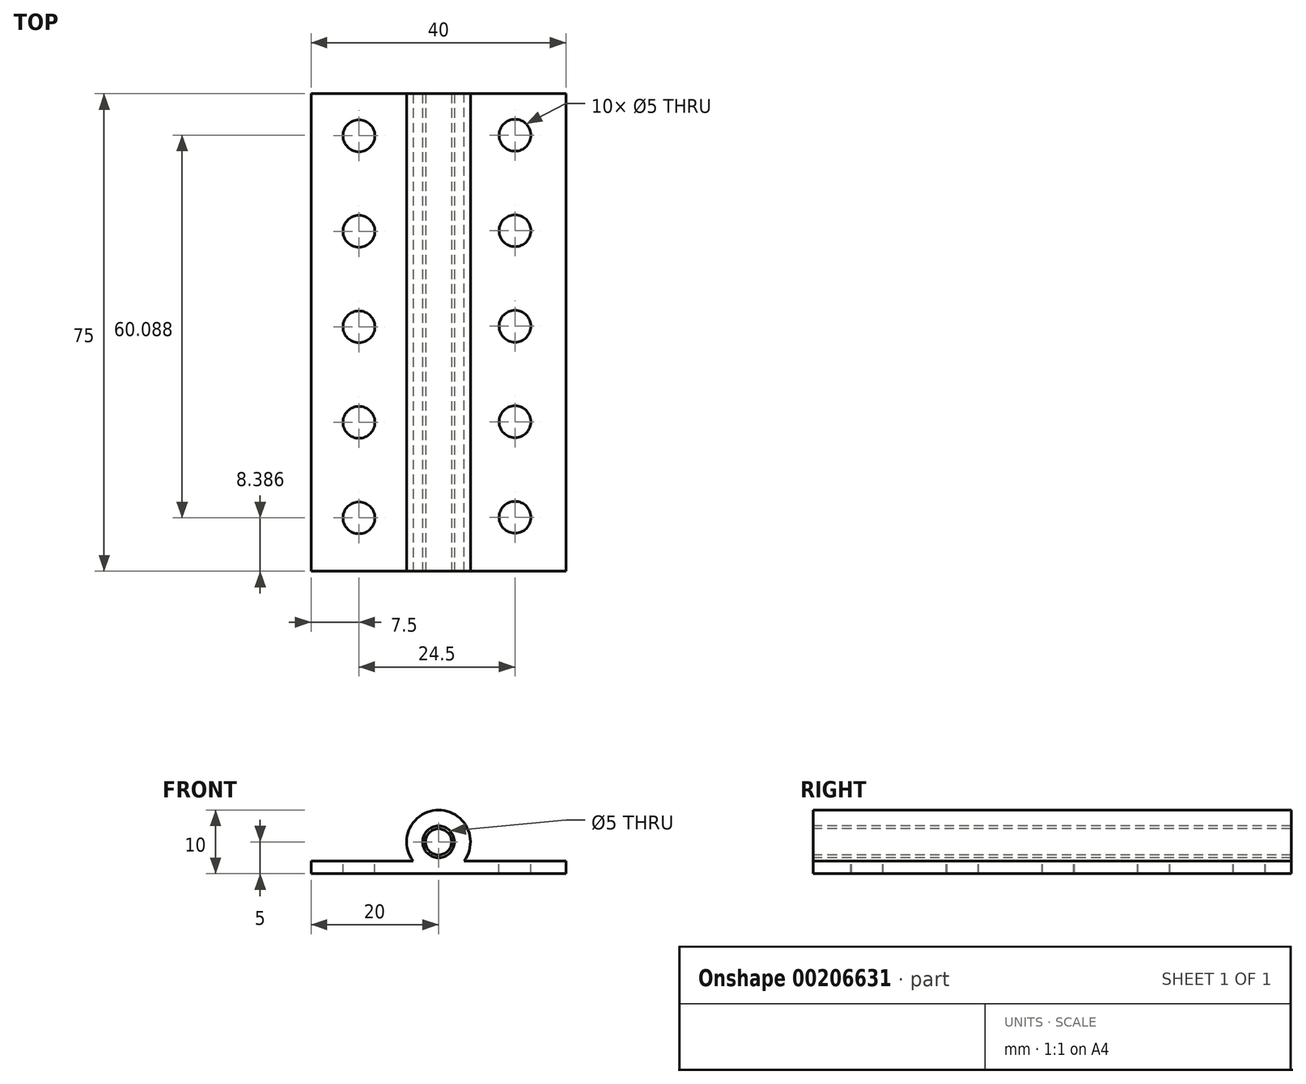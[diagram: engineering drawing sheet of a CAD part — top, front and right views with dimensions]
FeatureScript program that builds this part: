
annotation { "Feature Type Name" : "Feature", "Feature Type Description" : "" }
export const myFeature = defineFeature(function(context is Context, id is Id, definition is map)
    precondition{}
    {
        {
            var Q0;
            Q0=qCreatedBy(makeId("Front.planeOp"),FACE);
            var sketch = newSketch(context, id + "F0", { "sketchPlane" : qUnion([Q0])});
            skCircle(sketch, "E0", {"center": v(0, 0) * mm, "radius": 5 * mm});
            skSolve(sketch);
        }
        {
            var Q0;
            Q0=qCreatedBy(makeId("Front.planeOp"),FACE);
            var sketch = newSketch(context, id + "F1", { "sketchPlane" : qUnion([Q0])});
            skLineSegment(sketch, "E1.bottom", {"start": v(0, -5) * mm, "end": v(20, -5) * mm});
            skLineSegment(sketch, "E1.top", {"start": v(0, -3) * mm, "end": v(20, -3) * mm});
            skLineSegment(sketch, "E1.left", {"start": v(0, -5) * mm, "end": v(0, -3) * mm});
            skLineSegment(sketch, "E1.right", {"start": v(20, -5) * mm, "end": v(20, -3) * mm});
            skSolve(sketch);
        }
        {
            var Q0;
            Q0=makeQuery(id+"F0.imprint","IMPRINT",FACE,{"disambiguationData":[TD([[makeQuery(id+"F0.imprint","IMPRINT",EDGE,{"derivedFrom":sQuery(id+"F0.wireOp",EDGE,"E0")}),1.0]])]});
            var Q1;
            Q1=makeQuery(id+"F1.imprint","IMPRINT",FACE,{"disambiguationData":[TD([[makeQuery(id+"F1.imprint","IMPRINT",EDGE,{"derivedFrom":sQuery(id+"F1.wireOp",EDGE,"E1.bottom")}),1.0]])]});
            extrude(context, id + "F2", {"entities" : qUnion([Q0, Q1]), "depth" : 25 * mm});
        }
        {
            var Q0;
            Q0=makeQuery(id+"F2.opExtrude","CAP_FACE",FACE,{"disambiguationData":[OSD([sQuery(id+"F1.wireOp",EDGE,"E1.bottom"),sQuery(id+"F1.wireOp",EDGE,"E1.top"),sQuery(id+"F1.wireOp",EDGE,"E1.left"),sQuery(id+"F1.wireOp",EDGE,"E1.right")])],"isStart":false});
            extrude(context, id + "F3", {"entities" : qUnion([Q0]), "operationType" : NewBodyOperationType.ADD, "depth" : 25 * mm});
        }
        {
            var Q0;
            Q0=makeQuery(id+"F3.opExtrude","CAP_FACE",FACE,{"disambiguationData":[OSD([sQuery(id+"F1.wireOp",EDGE,"E1.bottom"),sQuery(id+"F1.wireOp",EDGE,"E1.top"),sQuery(id+"F1.wireOp",EDGE,"E1.left"),sQuery(id+"F1.wireOp",EDGE,"E1.right")])],"isStart":false});
            var sketch = newSketch(context, id + "F4", { "sketchPlane" : qUnion([Q0])});
            skCircle(sketch, "E2", {"center": v(0, 0) * mm, "radius": 5 * mm});
            skSolve(sketch);
        }
        {
            var Q0;
            {var subQ1=makeQuery(id+"F3.opExtrude","CAP_EDGE",EDGE,{"disambiguationData":[OSD([sQuery(id+"F1.wireOp",EDGE,"E1.bottom")])],"isStart":false});Q0=makeQuery(id+"F4.imprint","IMPRINT",FACE,{"disambiguationData":[TD([[makeQuery(id+"F4.imprint","IMPRINT",EDGE,{"derivedFrom":subQ1}),1.0]])]});}
            extrude(context, id + "F5", {"entities" : qUnion([Q0]), "operationType" : NewBodyOperationType.ADD, "depth" : 25 * mm});
        }
        {
            var Q0;
            Q0=qSketchRegion(id+"F4",true);
            extrude(context, id + "F6", {"entities" : qUnion([Q0]), "operationType" : NewBodyOperationType.ADD, "depth" : 25 * mm});
        }
        {
            var Q0;
            {var subQ0=sQuery(id+"F4.wireOp",EDGE,"E2");Q0=makeQuery(id+"F6.boolean.opBoolean","MERGE",FACE,{"derivedFrom":[makeQuery(id+"F5.opExtrude","CAP_FACE",FACE,{"disambiguationData":[OSD([sQuery(id+"F1.wireOp",EDGE,"E1.bottom"),sQuery(id+"F1.wireOp",EDGE,"E1.top"),sQuery(id+"F1.wireOp",EDGE,"E1.right"),subQ0])],"isStart":false}),makeQuery(id+"F6.opExtrude","CAP_FACE",FACE,{"disambiguationData":[OSD([subQ0])],"isStart":false})]});}
            var sketch = newSketch(context, id + "F7", { "sketchPlane" : qUnion([Q0])});
            skCircle(sketch, "E3", {"center": v(0, 0) * mm, "radius": 2.5 * mm});
            skSolve(sketch);
        }
        {
            var Q0;
            Q0=makeQuery(id+"F7.imprint","IMPRINT",FACE,{"disambiguationData":[TD([[makeQuery(id+"F7.imprint","IMPRINT",EDGE,{"derivedFrom":sQuery(id+"F7.wireOp",EDGE,"E3")}),1.0]])]});
            var Q1;
            Q1=sQuery(id+"F7.wireOp",EDGE,"E3");
            extrude(context, id + "F8", {"entities" : qUnion([Q0]), "operationType" : NewBodyOperationType.REMOVE, "surfaceEntities" : qUnion([Q1]), "oppositeDirection" : true, "depth" : 85.7 * mm});
        }
        {
            var Q0;
            Q0=makeQuery(id+"F2.opExtrude","CAP_FACE",FACE,{"disambiguationData":[OSD([sQuery(id+"F0.wireOp",EDGE,"E0")])],"isStart":false});
            extrude(context, id + "F9", {"entities" : qUnion([Q0]), "operationType" : NewBodyOperationType.REMOVE, "depth" : 25 * mm});
        }
        {
            var Q0;
            Q0=makeQuery(id+"F2.opExtrude","CAP_FACE",FACE,{"disambiguationData":[OSD([sQuery(id+"F0.wireOp",EDGE,"E0")])],"isStart":false});
            var sketch = newSketch(context, id + "F10", { "sketchPlane" : qUnion([Q0])});
            skCircle(sketch, "E4", {"center": v(0, 0) * mm, "radius": 5 * mm});
            skSolve(sketch);
        }
        {
            var Q0;
            Q0=qSketchRegion(id+"F10",true);
            extrude(context, id + "F11", {"entities" : qUnion([Q0]), "operationType" : NewBodyOperationType.REMOVE, "depth" : 25 * mm});
        }
        {
            var Q0;
            {var subQ0=sQuery(id+"F1.wireOp",EDGE,"E1.top");Q0=makeQuery(id+"F5.boolean.opBoolean","MERGE",FACE,{"derivedFrom":[makeQuery(id+"F3.boolean.opBoolean","MERGE",FACE,{"derivedFrom":[makeQuery(id+"F2.opExtrude","SWEPT_FACE",FACE,{"disambiguationData":[OSD([subQ0])]}),makeQuery(id+"F3.opExtrude","SWEPT_FACE",FACE,{"disambiguationData":[OSD([subQ0])]})]}),makeQuery(id+"F5.opExtrude","SWEPT_FACE",FACE,{"disambiguationData":[OSD([subQ0])]})]});}
            var sketch = newSketch(context, id + "F12", { "sketchPlane" : qUnion([Q0])});
            skCircle(sketch, "E5", {"center": v(12, -6.53) * mm, "radius": 2.5 * mm});
            skCircle(sketch, "E6", {"center": v(12, -21.53) * mm, "radius": 2.5 * mm});
            skCircle(sketch, "E7", {"center": v(12, -36.53) * mm, "radius": 2.5 * mm});
            skCircle(sketch, "E8", {"center": v(12, -51.53) * mm, "radius": 2.5 * mm});
            skCircle(sketch, "E9", {"center": v(12, -66.53) * mm, "radius": 2.5 * mm});
            skSolve(sketch);
        }
        {
            var Q0;
            Q0=makeQuery(id+"F12.imprint","IMPRINT",FACE,{"disambiguationData":[TD([[makeQuery(id+"F12.imprint","IMPRINT",EDGE,{"derivedFrom":sQuery(id+"F12.wireOp",EDGE,"E5")}),1.0]])]});
            var Q1;
            Q1=makeQuery(id+"F12.imprint","IMPRINT",FACE,{"disambiguationData":[TD([[makeQuery(id+"F12.imprint","IMPRINT",EDGE,{"derivedFrom":sQuery(id+"F12.wireOp",EDGE,"E6")}),1.0]])]});
            var Q2;
            Q2=makeQuery(id+"F12.imprint","IMPRINT",FACE,{"disambiguationData":[TD([[makeQuery(id+"F12.imprint","IMPRINT",EDGE,{"derivedFrom":sQuery(id+"F12.wireOp",EDGE,"E7")}),1.0]])]});
            var Q3;
            Q3=makeQuery(id+"F12.imprint","IMPRINT",FACE,{"disambiguationData":[TD([[makeQuery(id+"F12.imprint","IMPRINT",EDGE,{"derivedFrom":sQuery(id+"F12.wireOp",EDGE,"E8")}),1.0]])]});
            var Q4;
            Q4=makeQuery(id+"F12.imprint","IMPRINT",FACE,{"disambiguationData":[TD([[makeQuery(id+"F12.imprint","IMPRINT",EDGE,{"derivedFrom":sQuery(id+"F12.wireOp",EDGE,"E9")}),1.0]])]});
            var Q5;
            Q5=sQuery(id+"F12.wireOp",EDGE,"E5");
            var Q6;
            Q6=sQuery(id+"F12.wireOp",EDGE,"E6");
            var Q7;
            Q7=sQuery(id+"F12.wireOp",EDGE,"E7");
            var Q8;
            Q8=sQuery(id+"F12.wireOp",EDGE,"E8");
            var Q9;
            Q9=sQuery(id+"F12.wireOp",EDGE,"E9");
            extrude(context, id + "F13", {"entities" : qUnion([Q0, Q1, Q2, Q3, Q4]), "operationType" : NewBodyOperationType.REMOVE, "surfaceEntities" : qUnion([Q5, Q6, Q7, Q8, Q9]), "oppositeDirection" : true, "depth" : 25 * mm});
        }
        {
            var Q0;
            {var subQ0=sQuery(id+"F4.wireOp",EDGE,"E2");Q0=makeQuery(id+"F6.boolean.opBoolean","MERGE",FACE,{"derivedFrom":[makeQuery(id+"F5.opExtrude","CAP_FACE",FACE,{"disambiguationData":[OSD([sQuery(id+"F1.wireOp",EDGE,"E1.bottom"),sQuery(id+"F1.wireOp",EDGE,"E1.top"),sQuery(id+"F1.wireOp",EDGE,"E1.right"),subQ0])],"isStart":false}),makeQuery(id+"F6.opExtrude","CAP_FACE",FACE,{"disambiguationData":[OSD([subQ0])],"isStart":false})]});}
            var sketch = newSketch(context, id + "F14", { "sketchPlane" : qUnion([Q0])});
            skLineSegment(sketch, "E10.bottom", {"start": v(0, -5) * mm, "end": v(-20, -5) * mm});
            skLineSegment(sketch, "E10.top", {"start": v(0, -3) * mm, "end": v(-20, -3) * mm});
            skLineSegment(sketch, "E10.left", {"start": v(0, -5) * mm, "end": v(0, -3) * mm});
            skLineSegment(sketch, "E10.right", {"start": v(-20, -5) * mm, "end": v(-20, -3) * mm});
            skSolve(sketch);
        }
        {
            var Q0;
            {var subQ0=sQuery(id+"F14.wireOp",EDGE,"E10.bottom");Q0=makeQuery(id+"F14.imprint","IMPRINT",FACE,{"disambiguationData":[TD([[makeQuery(id+"F14.imprint","IMPRINT",EDGE,{"derivedFrom":subQ0}),-1.0]])]});}
            extrude(context, id + "F15", {"entities" : qUnion([Q0]), "oppositeDirection" : true, "depth" : 75 * mm});
        }
        {
            var Q0;
            Q0=makeQuery(id+"F11.boolean.opBoolean","MERGE",FACE,{"derivedFrom":[makeQuery(id+"F2.opExtrude","CAP_FACE",FACE,{"disambiguationData":[OSD([sQuery(id+"F0.wireOp",EDGE,"E0")])],"isStart":false}),makeQuery(id+"F11.opExtrude","CAP_FACE",FACE,{"disambiguationData":[OSD([sQuery(id+"F10.wireOp",EDGE,"E4")])],"isStart":true})]});
            extrude(context, id + "F16", {"entities" : qUnion([Q0]), "operationType" : NewBodyOperationType.ADD, "depth" : 25 * mm});
        }
        {
            var Q0;
            {var subQ0=sQuery(id+"F4.wireOp",EDGE,"E2");Q0=makeQuery(id+"F6.boolean.opBoolean","MERGE",FACE,{"derivedFrom":[makeQuery(id+"F5.opExtrude","CAP_FACE",FACE,{"disambiguationData":[OSD([sQuery(id+"F1.wireOp",EDGE,"E1.bottom"),sQuery(id+"F1.wireOp",EDGE,"E1.top"),sQuery(id+"F1.wireOp",EDGE,"E1.right"),subQ0])],"isStart":false}),makeQuery(id+"F6.opExtrude","CAP_FACE",FACE,{"disambiguationData":[OSD([subQ0])],"isStart":false})]});}
            var sketch = newSketch(context, id + "F17", { "sketchPlane" : qUnion([Q0])});
            skCircle(sketch, "E11", {"center": v(0, 0) * mm, "radius": 2.05 * mm});
            skSolve(sketch);
        }
        {
            var Q0;
            Q0=makeQuery(id+"F17.imprint","IMPRINT",FACE,{"disambiguationData":[TD([[makeQuery(id+"F17.imprint","IMPRINT",EDGE,{"derivedFrom":sQuery(id+"F17.wireOp",EDGE,"E11")}),1.0]])]});
            extrude(context, id + "F18", {"entities" : qUnion([Q0]), "oppositeDirection" : true, "depth" : 75 * mm});
        }
        {
            var Q0;
            Q0=makeQuery(id+"F15.opExtrude","SWEPT_FACE",FACE,{"disambiguationData":[OSD([sQuery(id+"F14.wireOp",EDGE,"E10.top")])]});
            var sketch = newSketch(context, id + "F19", { "sketchPlane" : qUnion([Q0])});
            skCircle(sketch, "E12", {"center": v(-12.5, -6.61) * mm, "radius": 2.5 * mm});
            skCircle(sketch, "E13", {"center": v(-12.5, -21.61) * mm, "radius": 2.5 * mm});
            skCircle(sketch, "E14", {"center": v(-12.5, -36.61) * mm, "radius": 2.5 * mm});
            skCircle(sketch, "E15", {"center": v(-12.5, -51.61) * mm, "radius": 2.5 * mm});
            skCircle(sketch, "E16", {"center": v(-12.5, -66.61) * mm, "radius": 2.5 * mm});
            skSolve(sketch);
        }
        {
            var Q0;
            Q0=makeQuery(id+"F19.imprint","IMPRINT",FACE,{"disambiguationData":[TD([[makeQuery(id+"F19.imprint","IMPRINT",EDGE,{"derivedFrom":sQuery(id+"F19.wireOp",EDGE,"E12")}),1.0]])]});
            var Q1;
            Q1=makeQuery(id+"F19.imprint","IMPRINT",FACE,{"disambiguationData":[TD([[makeQuery(id+"F19.imprint","IMPRINT",EDGE,{"derivedFrom":sQuery(id+"F19.wireOp",EDGE,"E13")}),1.0]])]});
            var Q2;
            Q2=makeQuery(id+"F19.imprint","IMPRINT",FACE,{"disambiguationData":[TD([[makeQuery(id+"F19.imprint","IMPRINT",EDGE,{"derivedFrom":sQuery(id+"F19.wireOp",EDGE,"E14")}),1.0]])]});
            var Q3;
            Q3=makeQuery(id+"F19.imprint","IMPRINT",FACE,{"disambiguationData":[TD([[makeQuery(id+"F19.imprint","IMPRINT",EDGE,{"derivedFrom":sQuery(id+"F19.wireOp",EDGE,"E15")}),1.0]])]});
            var Q4;
            Q4=makeQuery(id+"F19.imprint","IMPRINT",FACE,{"disambiguationData":[TD([[makeQuery(id+"F19.imprint","IMPRINT",EDGE,{"derivedFrom":sQuery(id+"F19.wireOp",EDGE,"E16")}),1.0]])]});
            extrude(context, id + "F20", {"entities" : qUnion([Q0, Q1, Q2, Q3, Q4]), "operationType" : NewBodyOperationType.REMOVE, "oppositeDirection" : true, "depth" : 25 * mm});
        }
    });
